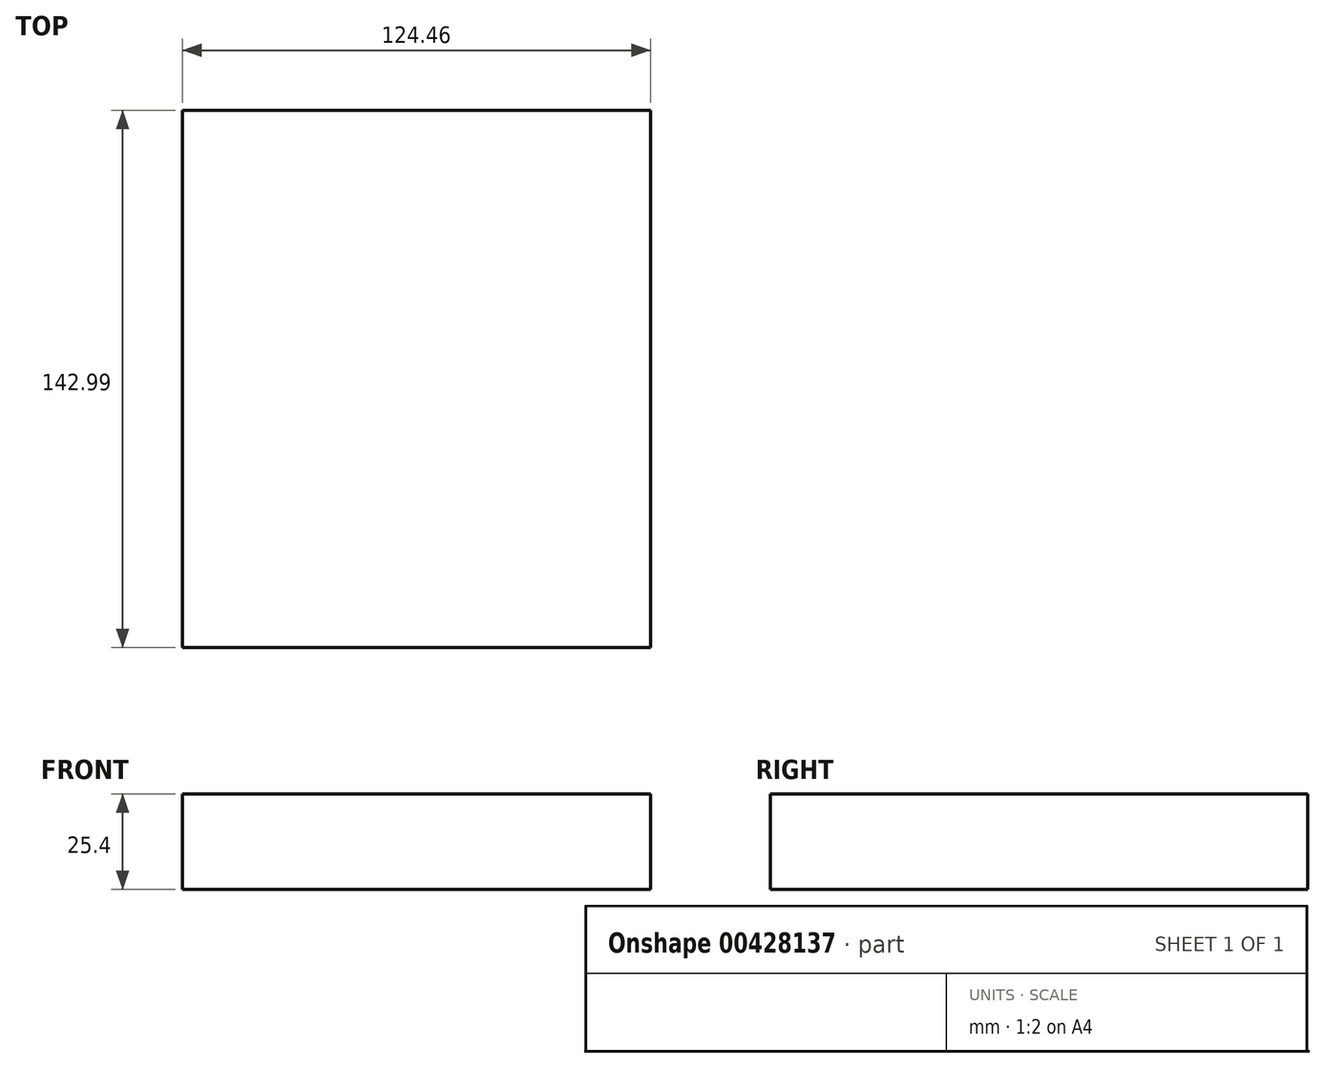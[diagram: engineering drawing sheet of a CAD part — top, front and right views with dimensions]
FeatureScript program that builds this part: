
annotation { "Feature Type Name" : "Feature", "Feature Type Description" : "" }
export const myFeature = defineFeature(function(context is Context, id is Id, definition is map)
    precondition{}
    {
        {
            var Q0;
            Q0=qCreatedBy(makeId("Top.planeOp"),FACE);
            var sketch = newSketch(context, id + "F0", { "sketchPlane" : qUnion([Q0])});
            skLineSegment(sketch, "E0", {"start": v(-7.47, 23.43) * mm, "end": v(52.56, -84) * mm});
            skLineSegment(sketch, "E1", {"start": v(52.56, -84) * mm, "end": v(37.33, -56.74) * mm});
            skLineSegment(sketch, "E2", {"start": v(37.33, -56.74) * mm, "end": v(0, 10.05) * mm});
            skLineSegment(sketch, "E3", {"start": v(0, 10.05) * mm, "end": v(-22.69, 149.36) * mm});
            skLineSegment(sketch, "E4.bottom", {"start": v(39.58, -103.94) * mm, "end": v(-84.88, -103.94) * mm});
            skLineSegment(sketch, "E4.top", {"start": v(39.58, 39.05) * mm, "end": v(-84.88, 39.05) * mm});
            skLineSegment(sketch, "E4.left", {"start": v(39.58, -103.94) * mm, "end": v(39.58, 39.05) * mm});
            skLineSegment(sketch, "E4.right", {"start": v(-84.88, -103.94) * mm, "end": v(-84.88, 39.05) * mm});
            skSolve(sketch);
        }
        {
            var Q0;
            Q0 = qSketchRegion(id + "F0", true);
            extrude(context, id + "F1", {"entities" : qUnion([Q0]), "depth" : 25.4 * mm});
        }
    });
